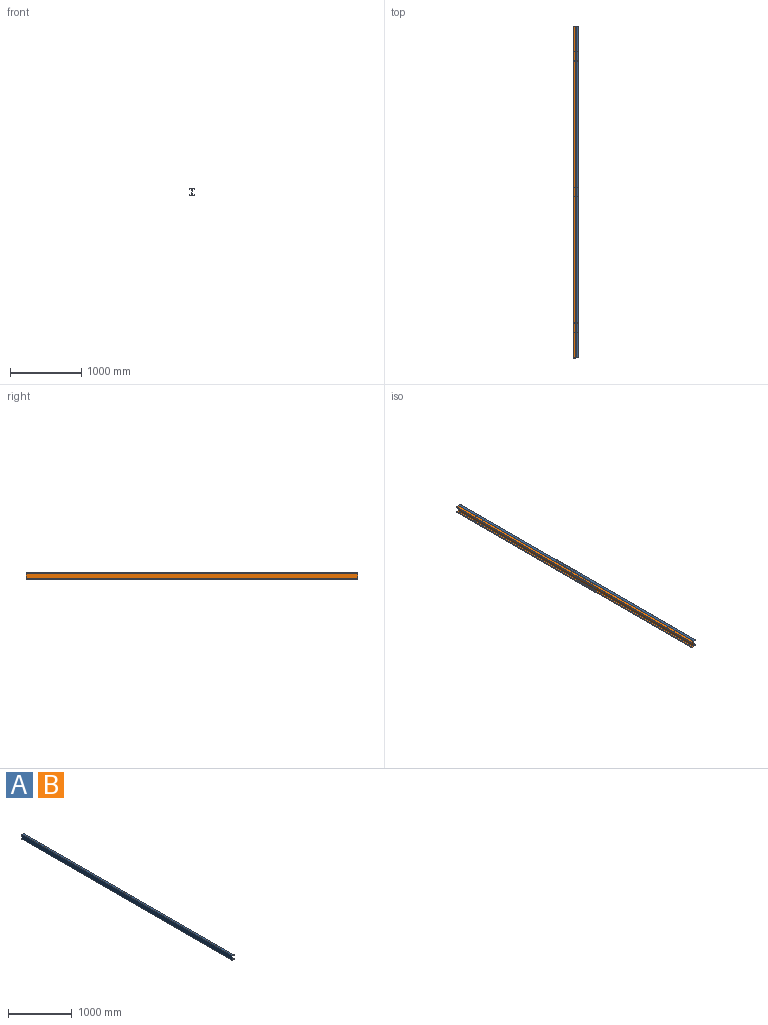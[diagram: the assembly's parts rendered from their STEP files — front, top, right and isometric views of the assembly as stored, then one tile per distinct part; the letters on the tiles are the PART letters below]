
ASSEMBLY  parts=2 mates=1
PART A: 26 faces, bbox 41.3x4673.6x92.1 mm
  f0: plane 4673.6x1.37mm, normal (0,0,1), area 6410.3mm2, adj f1,f11,f12,f13
  f1: plane 4673.6x14.5mm, normal (-1,0,0), area 67783.1mm2, adj f0,f2,f12,f13
  f2: plane 4673.6x38.53mm, normal (0,0,1), area 180034.7mm2, adj f1,f3,f12,f13,f14,f15,f16,f17
  f3: plane 4673.6x89.33mm, normal (1,0,0), area 417501.1mm2, adj f2,f4,f12,f13
  f4: plane 4673.6x38.53mm, normal (0,0,-1), area 180034.7mm2, adj f3,f5,f12,f13,f20,f21,f22,f23
  f5: plane 4673.6x14.5mm, normal (-1,0,0), area 67783.1mm2, adj f4,f6,f12,f13
  f6: plane 4673.6x1.37mm, normal (0,0,-1), area 6410.3mm2, adj f5,f7,f12,f13
  f7: plane 4673.6x15.88mm, normal (1,0,0), area 74193.4mm2, adj f6,f8,f12,f13
  f8: plane 4673.6x41.28mm, normal (0,0,1), area 192855.3mm2, adj f7,f9,f12,f13,f20,f21,f22,f23
  f9: plane 4673.6x92.08mm, normal (-1,0,0), area 430321.7mm2, adj f8,f10,f12,f13
  f10: plane 4673.6x41.28mm, normal (0,0,-1), area 192855.3mm2, adj f9,f11,f12,f13,f14,f15,f16,f17
  f11: plane 4673.6x15.88mm, normal (1,0,0), area 74193.4mm2, adj f0,f10,f12,f13
  f12: plane 92.08x41.28mm, normal (0,-1,0), area 275.5mm2, adj f0,f1,f2,f3,f4,f5,f6,f7
  f13: plane 92.08x41.28mm, normal (0,1,0), area 275.5mm2, adj f0,f1,f2,f3,f4,f5,f6,f7
  f14: cylinder r=1.59mm len=3.18mm, axis (0,0,1), area 13.7mm2, adj f2,f10
  f15: cylinder r=1.59mm len=3.18mm, axis (0,0,1), area 13.7mm2, adj f2,f10
  f16: cylinder r=1.59mm len=3.18mm, axis (0,0,1), area 13.7mm2, adj f2,f10
  f17: cylinder r=1.59mm len=3.18mm, axis (0,0,1), area 13.7mm2, adj f2,f10
  f18: cylinder r=1.59mm len=3.18mm, axis (0,0,1), area 13.7mm2, adj f2,f10
  f19: cylinder r=1.59mm len=3.18mm, axis (0,0,1), area 13.7mm2, adj f2,f10
  f20: cylinder r=1.59mm len=3.18mm, axis (0,0,1), area 13.7mm2, adj f4,f8
  f21: cylinder r=1.59mm len=3.18mm, axis (0,0,1), area 13.7mm2, adj f4,f8
  f22: cylinder r=1.59mm len=3.18mm, axis (0,0,1), area 13.7mm2, adj f4,f8
  f23: cylinder r=1.59mm len=3.18mm, axis (0,0,1), area 13.7mm2, adj f4,f8
  f24: cylinder r=1.59mm len=3.18mm, axis (0,0,1), area 13.7mm2, adj f4,f8
  f25: cylinder r=1.59mm len=3.18mm, axis (0,0,1), area 13.7mm2, adj f4,f8
PART B: same geometry as A
PLACE A t=(-1690.85,660.71,-753.07)mm
PLACE B rot(axis=(0,1,0),180deg) t=(-1971.82,660.71,-1138.98)mm
MATE fastened B.f9 <-> A.f9  axis (1,0,0) through (-1831.34,-4012.89,-946.02)mm
